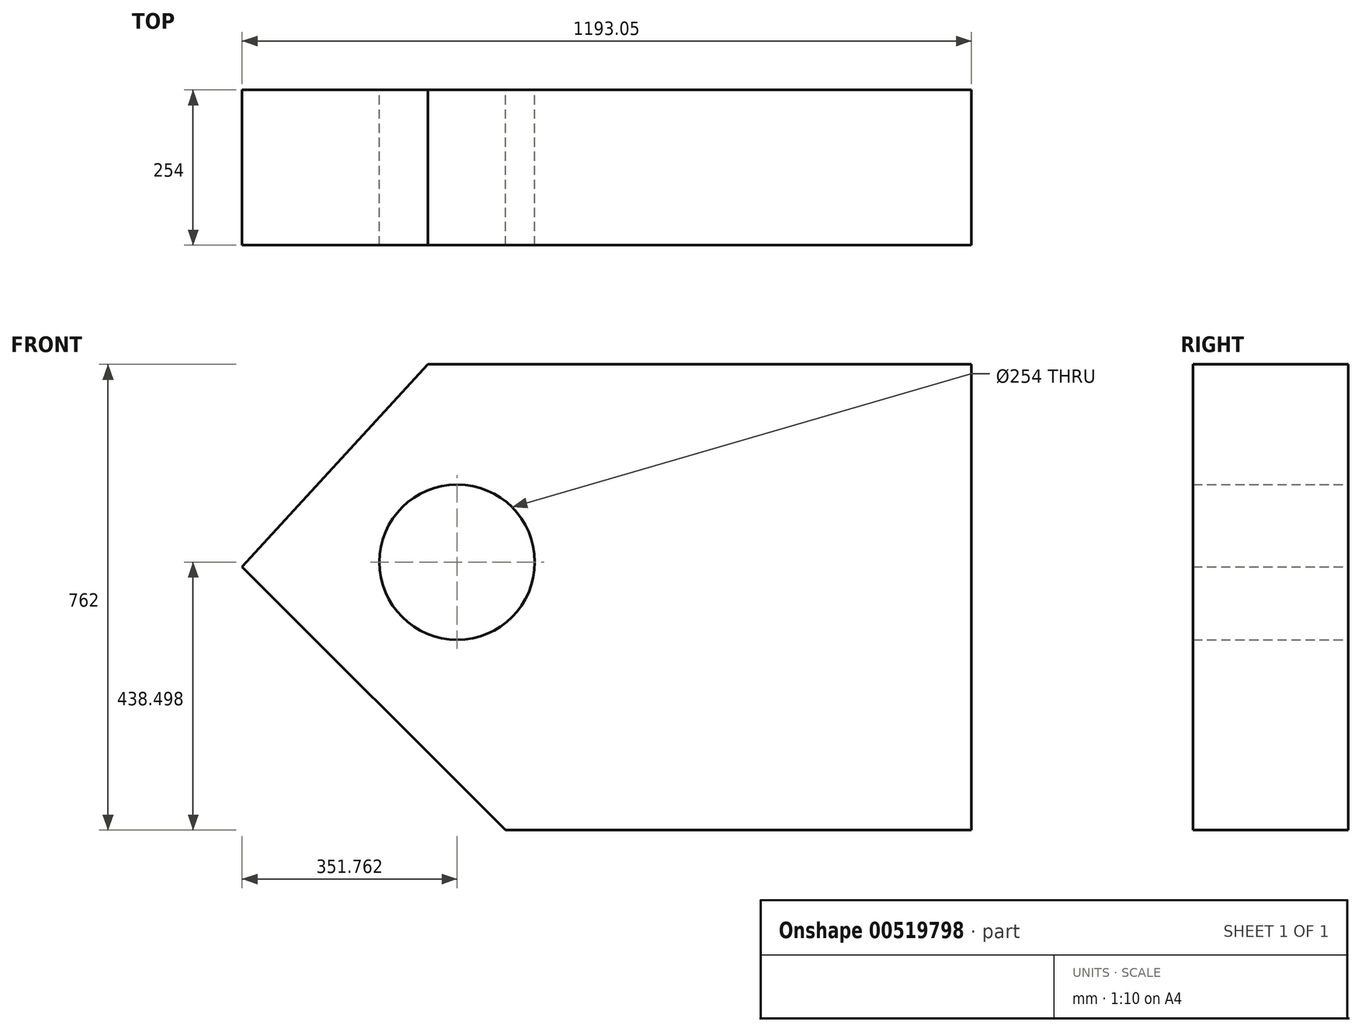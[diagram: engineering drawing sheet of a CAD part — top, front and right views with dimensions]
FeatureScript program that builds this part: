
annotation { "Feature Type Name" : "Feature", "Feature Type Description" : "" }
export const myFeature = defineFeature(function(context is Context, id is Id, definition is map)
    precondition{}
    {
        {
            var Q0;
            Q0=qCreatedBy(makeId("Front.planeOp"),FACE);
            var sketch = newSketch(context, id + "F0", { "sketchPlane" : qUnion([Q0])});
            skLineSegment(sketch, "E0", {"start": v(0, 0) * mm, "end": v(889, 0) * mm});
            skLineSegment(sketch, "E1", {"start": v(889, 0) * mm, "end": v(889, -762) * mm});
            skLineSegment(sketch, "E2", {"start": v(889, -762) * mm, "end": v(127, -762) * mm});
            skLineSegment(sketch, "E3", {"start": v(127, -762) * mm, "end": v(-304.05, -330.95) * mm});
            skLineSegment(sketch, "E4", {"start": v(-304.05, -330.95) * mm, "end": v(0, 0) * mm});
            skCircle(sketch, "E5", {"center": v(47.71, -323.5) * mm, "radius": 127 * mm});
            skSolve(sketch);
        }
        {
            var Q0;
            Q0=makeQuery(id+"F0.imprint","IMPRINT",FACE,{"disambiguationData":[TD([[makeQuery(id+"F0.imprint","IMPRINT",EDGE,{"derivedFrom":sQuery(id+"F0.wireOp",EDGE,"E0")}),-1.0]])]});
            extrude(context, id + "F1", {"entities" : qUnion([Q0]), "depth" : 254 * mm, "offsetDistance" : 25.4 * mm});
        }
    });
